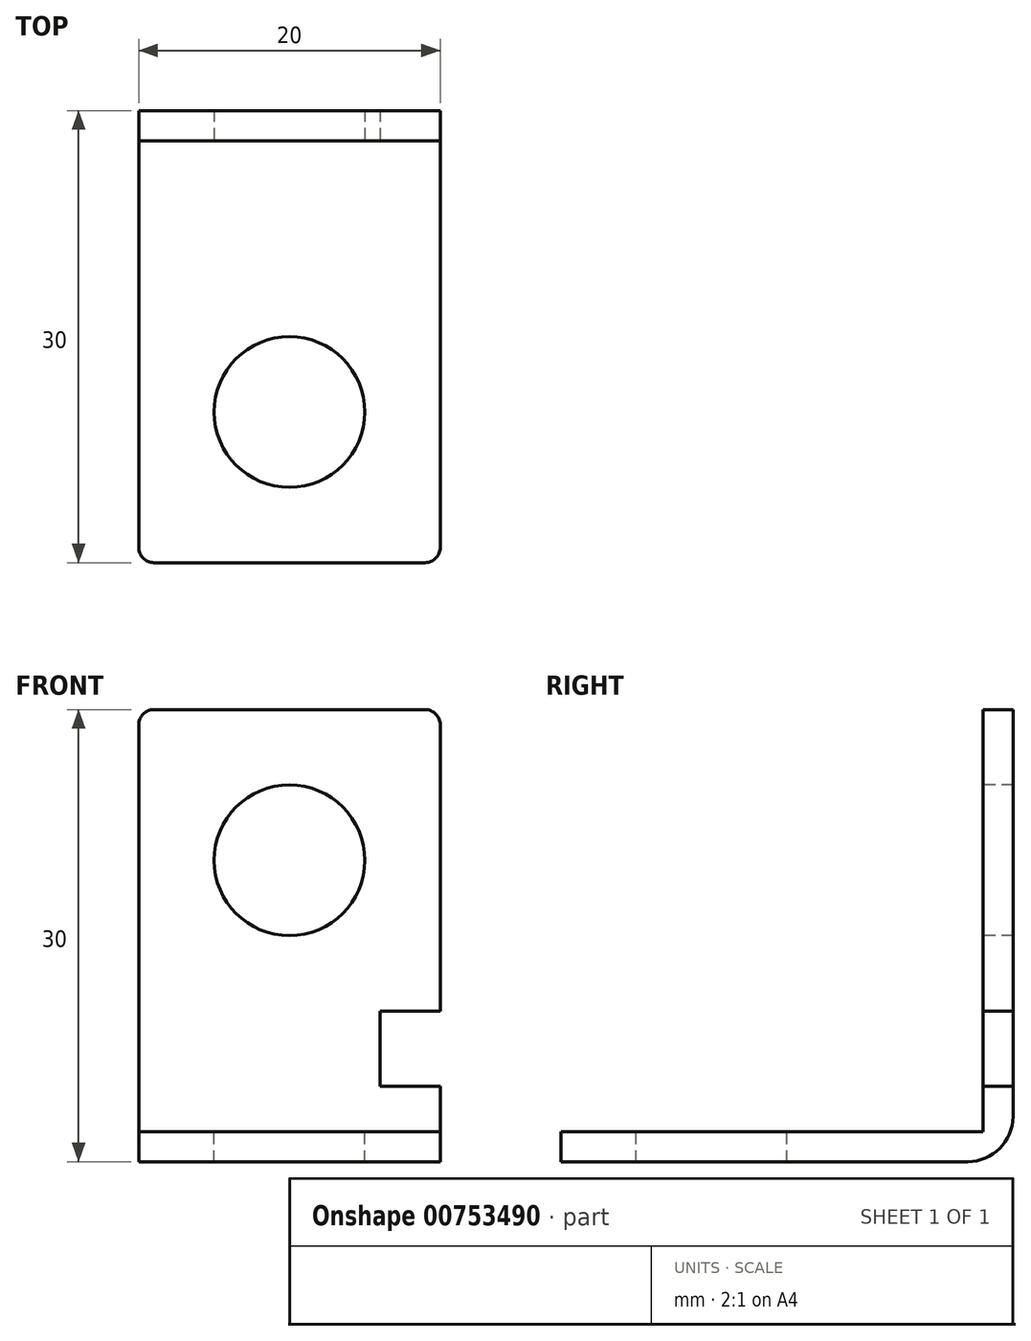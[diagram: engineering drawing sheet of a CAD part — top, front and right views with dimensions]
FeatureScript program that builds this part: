
annotation { "Feature Type Name" : "Feature", "Feature Type Description" : "" }
export const myFeature = defineFeature(function(context is Context, id is Id, definition is map)
    precondition{}
    {
        {
            var Q0;
            Q0=qCreatedBy(makeId("Top.planeOp"),FACE);
            var sketch = newSketch(context, id + "F0", { "sketchPlane" : qUnion([Q0])});
            skLineSegment(sketch, "E0.bottom", {"start": v(0, 0) * mm, "end": v(20, 0) * mm});
            skLineSegment(sketch, "E0.top", {"start": v(0, 30) * mm, "end": v(20, 30) * mm});
            skLineSegment(sketch, "E0.left", {"start": v(0, 0) * mm, "end": v(0, 30) * mm});
            skLineSegment(sketch, "E0.right", {"start": v(20, 0) * mm, "end": v(20, 30) * mm});
            skSolve(sketch);
        }
        {
            var Q0;
            Q0 = qSketchRegion(id + "F0", true);
            extrude(context, id + "F1", {"entities" : qUnion([Q0]), "depth" : 2 * mm, "offsetDistance" : 25 * mm});
        }
        {
            var Q0;
            Q0=makeQuery(id+"F1.opExtrude","CAP_FACE",FACE,{"disambiguationData":[OSD([sQuery(id+"F0.wireOp",EDGE,"E0.bottom"),sQuery(id+"F0.wireOp",EDGE,"E0.top"),sQuery(id+"F0.wireOp",EDGE,"E0.left"),sQuery(id+"F0.wireOp",EDGE,"E0.right")])],"isStart":false});
            var sketch = newSketch(context, id + "F2", { "sketchPlane" : qUnion([Q0])});
            skLineSegment(sketch, "E1.bottom", {"start": v(0, 30) * mm, "end": v(20, 30) * mm});
            skLineSegment(sketch, "E1.top", {"start": v(0, 28) * mm, "end": v(20, 28) * mm});
            skLineSegment(sketch, "E1.left", {"start": v(0, 30) * mm, "end": v(0, 28) * mm});
            skLineSegment(sketch, "E1.right", {"start": v(20, 30) * mm, "end": v(20, 28) * mm});
            skSolve(sketch);
        }
        {
            var Q0;
            Q0 = qSketchRegion(id + "F2", true);
            extrude(context, id + "F3", {"entities" : qUnion([Q0]), "operationType" : NewBodyOperationType.ADD, "depth" : 28 * mm, "offsetDistance" : 25 * mm});
        }
        {
            var Q0;
            Q0=makeQuery(id+"F1.opExtrude","CAP_FACE",FACE,{"disambiguationData":[OSD([sQuery(id+"F0.wireOp",EDGE,"E0.bottom"),sQuery(id+"F0.wireOp",EDGE,"E0.top"),sQuery(id+"F0.wireOp",EDGE,"E0.left"),sQuery(id+"F0.wireOp",EDGE,"E0.right")])],"isStart":false});
            var sketch = newSketch(context, id + "F4", { "sketchPlane" : qUnion([Q0])});
            skCircle(sketch, "E2", {"center": v(10, 10) * mm, "radius": 5 * mm});
            skSolve(sketch);
        }
        {
            var Q0;
            Q0 = qSketchRegion(id + "F4", true);
            extrude(context, id + "F5", {"entities" : qUnion([Q0]), "operationType" : NewBodyOperationType.REMOVE, "endBound" : BoundingType.THROUGH_ALL, "oppositeDirection" : true, "depth" : 25 * mm, "offsetDistance" : 25 * mm});
        }
        {
            var Q0;
            Q0=makeQuery(id+"F3.opExtrude","SWEPT_FACE",FACE,{"disambiguationData":[OSD([sQuery(id+"F2.wireOp",EDGE,"E1.top")])]});
            var sketch = newSketch(context, id + "F6", { "sketchPlane" : qUnion([Q0])});
            skCircle(sketch, "E3", {"center": v(10, 20) * mm, "radius": 5 * mm});
            skSolve(sketch);
        }
        {
            var Q0;
            Q0 = qSketchRegion(id + "F6", true);
            extrude(context, id + "F7", {"entities" : qUnion([Q0]), "operationType" : NewBodyOperationType.REMOVE, "endBound" : BoundingType.THROUGH_ALL, "oppositeDirection" : true, "depth" : 25 * mm, "offsetDistance" : 25 * mm});
        }
        {
            var Q0;
            Q0=makeQuery(id+"F3.opExtrude","SWEPT_FACE",FACE,{"disambiguationData":[OSD([sQuery(id+"F2.wireOp",EDGE,"E1.top")])]});
            var sketch = newSketch(context, id + "F8", { "sketchPlane" : qUnion([Q0])});
            skLineSegment(sketch, "E4.bottom", {"start": v(20, 10) * mm, "end": v(16, 10) * mm});
            skLineSegment(sketch, "E4.top", {"start": v(20, 5) * mm, "end": v(16, 5) * mm});
            skLineSegment(sketch, "E4.left", {"start": v(20, 10) * mm, "end": v(20, 5) * mm});
            skLineSegment(sketch, "E4.right", {"start": v(16, 10) * mm, "end": v(16, 5) * mm});
            skSolve(sketch);
        }
        {
            var Q0;
            Q0 = qSketchRegion(id + "F8", true);
            extrude(context, id + "F9", {"entities" : qUnion([Q0]), "operationType" : NewBodyOperationType.REMOVE, "endBound" : BoundingType.THROUGH_ALL, "oppositeDirection" : true, "depth" : 25 * mm, "offsetDistance" : 25 * mm});
        }
        {
            var Q0;
            Q0=makeQuery(id+"F1.opExtrude","SWEPT_EDGE",EDGE,{"disambiguationData":[OSD([sQuery(id+"F0.wireOp",EDGE,"E0.bottom"),sQuery(id+"F0.wireOp",EDGE,"E0.left")])]});
            var Q1;
            Q1=makeQuery(id+"F1.opExtrude","SWEPT_EDGE",EDGE,{"disambiguationData":[OSD([sQuery(id+"F0.wireOp",EDGE,"E0.bottom"),sQuery(id+"F0.wireOp",EDGE,"E0.right")])]});
            var Q2;
            Q2=makeQuery(id+"F3.opExtrude","CAP_EDGE",EDGE,{"disambiguationData":[OSD([sQuery(id+"F2.wireOp",EDGE,"E1.right")])],"isStart":false});
            var Q3;
            Q3=makeQuery(id+"F3.opExtrude","CAP_EDGE",EDGE,{"disambiguationData":[OSD([sQuery(id+"F2.wireOp",EDGE,"E1.left")])],"isStart":false});
            var Q4;
            Q4=makeQuery(id+"F3.opExtrude","CAP_EDGE",EDGE,{"disambiguationData":[OSD([sQuery(id+"F2.wireOp",EDGE,"E1.top")])],"isStart":true});
            fillet(context, id + "F10", {"entities" : qUnion([Q0, Q1, Q2, Q3, Q4]), "radius" : 1 * mm, "tangentPropagation" : true, "allowEdgeOverflow" : false});
        }
        {
            var Q0;
            Q0=makeQuery(id+"F1.opExtrude","CAP_EDGE",EDGE,{"disambiguationData":[OSD([sQuery(id+"F0.wireOp",EDGE,"E0.top")])],"isStart":true});
            fillet(context, id + "F11", {"entities" : qUnion([Q0]), "radius" : 3 * mm, "tangentPropagation" : true, "allowEdgeOverflow" : false});
        }
    });
